# Revit family: BVN_EF
name_source: partatom
category: Mechanical Equipment
units: mm (PartAtom-declared; Revit-internal decimal feet)

## family parameters
Always vertical = Yes
Cut with Voids When Loaded = No
Host = Wall
Part Type = Normal
Room Calculation Point = No
Round Connector Dimension = Use Diameter
Shared = No

## types (3) — shared parameters
Current = 0
Description = Plastic Fan
Frequency = 50 Hz
Insulation Class = B
Manufacturer = http://www.bahcivanmotor.com.tr
Model = EF
Protection Class = 20
URL = http://www.bahcivanmotor.com.tr
Voltage = 230 V

## per-type parameters (varying)
| type | A | Air Flow | B | C | D | E | E' | E'' | Material Cover | Material Fan | Pieces In Box | Power | Sound Pressure | Speed(d/d) | Weight |
| EF 1009 | 160 mm  [stored 0.524934 ft] | 100.00 m³/h | 160 mm  [stored 0.524934 ft] | -12 mm  [stored -0.0393701 ft] | 70 mm  [stored 0.229659 ft] | 98 mm | 138 mm | 88 mm | Stainless Steel | Stainless Steel | 24 | 13 W | 40 | 2600 | 0.50 kg |
| EF 1219 | 188 mm  [stored 0.616798 ft] | 200.00 m³/h | 188 mm  [stored 0.616798 ft] | -14 mm  [stored -0.0459318 ft] | 76 mm  [stored 0.249344 ft] | 118 mm | 158 mm | 108 mm | Default | <By Category> | 20 | 14 W | 41 | 2400 | 0.55 kg |
| EF 1530 | 208 mm | 300.00 m³/h | 208 mm | -14 mm  [stored -0.0459318 ft] | 118 mm | 145 mm  [stored 0.475722 ft] | 185 mm  [stored 0.606955 ft] | 135 mm  [stored 0.442913 ft] | Default | <By Category> | 16 | 21 W | 43 | 2000 | 0.71 kg |

note: source unit labels omitted for Current — the stored unit's dimension contradicts the parameter name (converter mislabeling)

note: [stored X ft] marks values corroborated as IEEE doubles in the binary element streams (Revit-internal decimal feet)

## geometry (parser evidence)
native form markers: Sweep x2
no freeform markers — native parametric forms only
